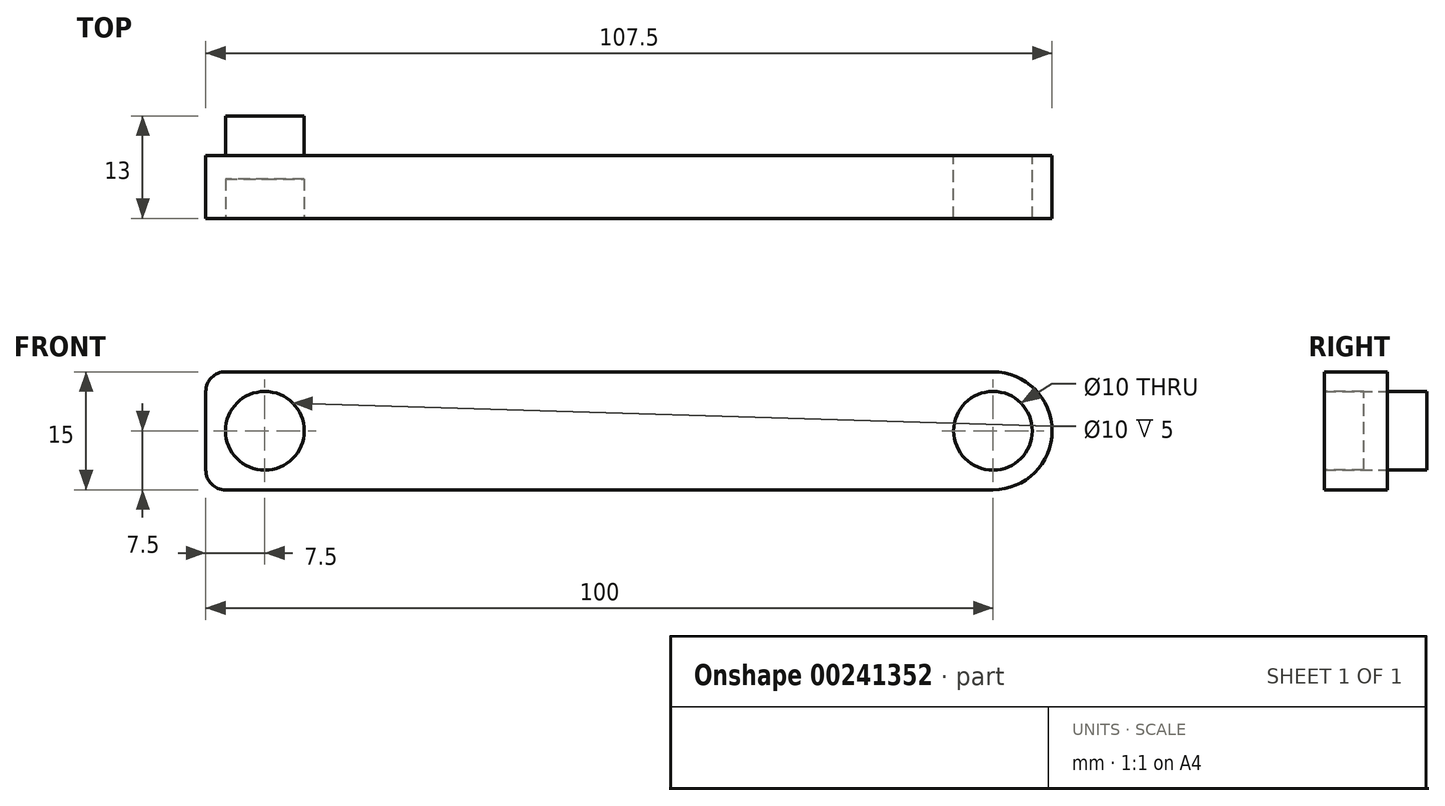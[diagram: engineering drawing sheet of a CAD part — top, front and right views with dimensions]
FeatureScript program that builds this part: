
annotation { "Feature Type Name" : "Feature", "Feature Type Description" : "" }
export const myFeature = defineFeature(function(context is Context, id is Id, definition is map)
    precondition{}
    {
        {
            var Q0;
            Q0=qCreatedBy(makeId("Front.planeOp"),FACE);
            var sketch = newSketch(context, id + "F0", { "sketchPlane" : qUnion([Q0])});
            skCircle(sketch, "E0", {"center": v(0, 0) * mm, "radius": 7.5 * mm});
            skCircle(sketch, "E1", {"center": v(0, 0) * mm, "radius": 5 * mm});
            skLineSegment(sketch, "E2.bottom", {"start": v(0, 7.5) * mm, "end": v(-100, 7.5) * mm});
            skLineSegment(sketch, "E2.top", {"start": v(0, -7.5) * mm, "end": v(-100, -7.5) * mm});
            skLineSegment(sketch, "E2.left", {"start": v(0, 7.5) * mm, "end": v(0, -7.5) * mm});
            skLineSegment(sketch, "E2.right", {"start": v(-100, 7.5) * mm, "end": v(-100, -7.5) * mm});
            skSolve(sketch);
        }
        {
            var Q0;
            {var subQ1=sQuery(id+"F0.wireOp",EDGE,"NwCUDoeX-6FFx-rpG8-aocx-gNc1TtZu7neD");Q0=makeQuery(id+"F0.imprint","IMPRINT",FACE,{"disambiguationData":[TD([[makeQuery(id+"F0.imprint","IMPRINT",EDGE,{"derivedFrom":subQ1}),-1.0]])]});}
            var Q1;
            {var subQ0=sQuery(id+"F0.wireOp",EDGE,"pMUDdTaR-RGpa-3EbT-v0LG-Nu6DOzsx8AzA");var subQ4=sQuery(id+"F0.wireOp",EDGE,"IL5Tp1Po-sgq1-uV5f-WThu-FCOuGZ4YDNK1");var subQ5=makeQuery(id+"F0.imprint","INTERSECT",VERTEX,{"disambiguationData":[OD(0.0)],"derivedFrom":[subQ4,subQ0]});Q1=makeQuery(id+"F0.imprint","IMPRINT",FACE,{"disambiguationData":[TD([[makeQuery(id+"F0.imprint","IMPRINT",EDGE,{"disambiguationData":[TD([[subQ5,-1.0]])],"derivedFrom":subQ4}),-1.0]])]});}
            var Q2;
            {var subQ0=sQuery(id+"F0.wireOp",EDGE,"pMUDdTaR-RGpa-3EbT-v0LG-Nu6DOzsx8AzA");var subQ4=sQuery(id+"F0.wireOp",EDGE,"IL5Tp1Po-sgq1-uV5f-WThu-FCOuGZ4YDNK1");var subQ5=makeQuery(id+"F0.imprint","INTERSECT",VERTEX,{"disambiguationData":[OD(0.0)],"derivedFrom":[subQ4,subQ0]});Q2=makeQuery(id+"F0.imprint","IMPRINT",FACE,{"disambiguationData":[TD([[makeQuery(id+"F0.imprint","IMPRINT",EDGE,{"disambiguationData":[TD([[subQ5,1.0]])],"derivedFrom":subQ4}),-1.0]])]});}
            var Q3;
            {var subQ1=sQuery(id+"F0.wireOp",EDGE,"E2.bottom");Q3=makeQuery(id+"F0.imprint","IMPRINT",FACE,{"disambiguationData":[TD([[makeQuery(id+"F0.imprint","IMPRINT",EDGE,{"derivedFrom":subQ1}),1.0]])]});}
            var Q4;
            {var subQ0=sQuery(id+"F0.wireOp",EDGE,"E2.left");var subQ4=sQuery(id+"F0.wireOp",EDGE,"E1");var subQ5=makeQuery(id+"F0.imprint","INTERSECT",VERTEX,{"disambiguationData":[OD(0.0)],"derivedFrom":[subQ4,subQ0]});Q4=makeQuery(id+"F0.imprint","IMPRINT",FACE,{"disambiguationData":[TD([[makeQuery(id+"F0.imprint","IMPRINT",EDGE,{"disambiguationData":[TD([[subQ5,-1.0]])],"derivedFrom":subQ4}),-1.0]])]});}
            var Q5;
            {var subQ0=sQuery(id+"F0.wireOp",EDGE,"E2.left");var subQ4=sQuery(id+"F0.wireOp",EDGE,"E1");var subQ5=makeQuery(id+"F0.imprint","INTERSECT",VERTEX,{"disambiguationData":[OD(0.0)],"derivedFrom":[subQ4,subQ0]});Q5=makeQuery(id+"F0.imprint","IMPRINT",FACE,{"disambiguationData":[TD([[makeQuery(id+"F0.imprint","IMPRINT",EDGE,{"disambiguationData":[TD([[subQ5,1.0]])],"derivedFrom":subQ4}),-1.0]])]});}
            extrude(context, id + "F1", {"entities" : qUnion([Q0, Q1, Q2, Q3, Q4, Q5]), "depth" : 8 * mm});
        }
        {
            var Q0;
            Q0=makeQuery(id+"F1.opExtrude","SWEPT_EDGE",EDGE,{"disambiguationData":[OSD([sQuery(id+"F0.wireOp",EDGE,"E2.bottom"),sQuery(id+"F0.wireOp",EDGE,"E2.right")])]});
            var Q1;
            Q1=makeQuery(id+"F1.opExtrude","SWEPT_EDGE",EDGE,{"disambiguationData":[OSD([sQuery(id+"F0.wireOp",EDGE,"E2.top"),sQuery(id+"F0.wireOp",EDGE,"E2.right")])]});
            fillet(context, id + "F2", {"entities" : qUnion([Q0, Q1]), "radius" : 2.5 * mm, "tangentPropagation" : true, "allowEdgeOverflow" : false});
        }
        {
            var Q0;
            Q0=makeQuery(id+"F1.opExtrude","CAP_FACE",FACE,{"disambiguationData":[OSD([sQuery(id+"F0.wireOp",EDGE,"E0"),sQuery(id+"F0.wireOp",EDGE,"E1"),sQuery(id+"F0.wireOp",EDGE,"E2.bottom"),sQuery(id+"F0.wireOp",EDGE,"E2.top"),sQuery(id+"F0.wireOp",EDGE,"E2.right")])],"isStart":true});
            var sketch = newSketch(context, id + "F3", { "sketchPlane" : qUnion([Q0])});
            skCircle(sketch, "E3", {"center": v(92.5, 0) * mm, "radius": 5 * mm});
            skSolve(sketch);
        }
        {
            var Q0;
            Q0=qSketchRegion(id+"F3",true);
            extrude(context, id + "F4", {"entities" : qUnion([Q0]), "operationType" : NewBodyOperationType.ADD, "depth" : 5 * mm});
        }
        {
            var Q0;
            Q0=makeQuery(id+"F1.opExtrude","CAP_FACE",FACE,{"disambiguationData":[OSD([sQuery(id+"F0.wireOp",EDGE,"E0"),sQuery(id+"F0.wireOp",EDGE,"E1"),sQuery(id+"F0.wireOp",EDGE,"E2.bottom"),sQuery(id+"F0.wireOp",EDGE,"E2.top"),sQuery(id+"F0.wireOp",EDGE,"E2.right")])],"isStart":false});
            var sketch = newSketch(context, id + "F5", { "sketchPlane" : qUnion([Q0])});
            skCircle(sketch, "E4", {"center": v(-92.5, 0) * mm, "radius": 5 * mm});
            skSolve(sketch);
        }
        {
            var Q0;
            Q0=qSketchRegion(id+"F5",true);
            extrude(context, id + "F6", {"entities" : qUnion([Q0]), "operationType" : NewBodyOperationType.REMOVE, "oppositeDirection" : true, "depth" : 5 * mm});
        }
    });
